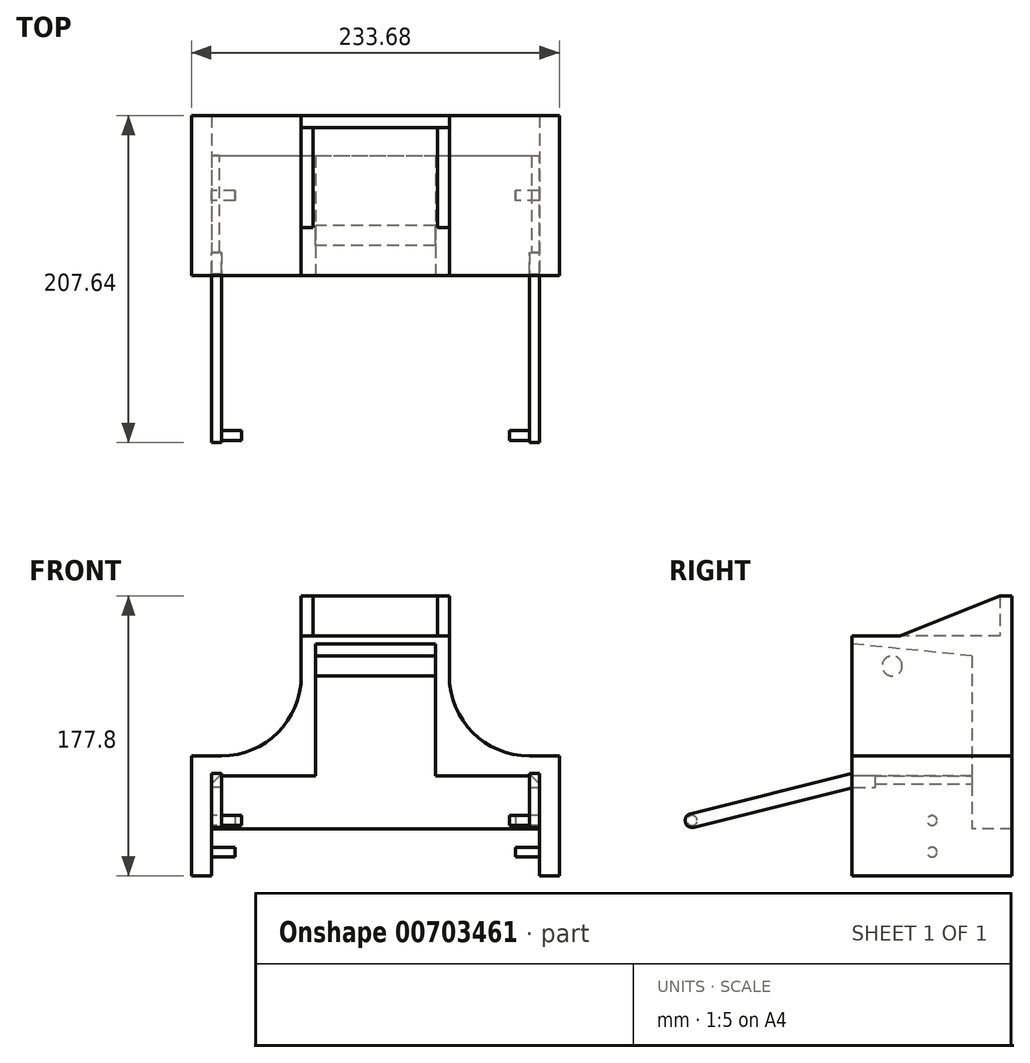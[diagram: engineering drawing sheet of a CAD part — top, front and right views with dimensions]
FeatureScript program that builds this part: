
annotation { "Feature Type Name" : "Feature", "Feature Type Description" : "" }
export const myFeature = defineFeature(function(context is Context, id is Id, definition is map)
    precondition{}
    {
        {
            var Q0;
            Q0=qCreatedBy(makeId("Front.planeOp"),FACE);
            var sketch = newSketch(context, id + "F0", { "sketchPlane" : qUnion([Q0])});
            skLineSegment(sketch, "E0.bottom", {"start": v(116.84, 76.2) * mm, "end": v(-116.84, 76.2) * mm});
            skLineSegment(sketch, "E0.top", {"start": v(116.84, -76.2) * mm, "end": v(-116.84, -76.2) * mm});
            skLineSegment(sketch, "E0.left", {"start": v(116.84, 76.2) * mm, "end": v(116.84, -76.2) * mm});
            skLineSegment(sketch, "E0.right", {"start": v(-116.84, 76.2) * mm, "end": v(-116.84, -76.2) * mm});
            skPoint(sketch, "E0.middle", {"position": v(0, 0) * mm});
            skLineSegment(sketch, "E1", {"start": v(-116.84, 0) * mm, "end": v(0, 0) * mm});
            skLineSegment(sketch, "E2", {"start": v(116.84, 0) * mm, "end": v(0, 0) * mm});
            skLineSegment(sketch, "E3", {"start": v(0, 76.2) * mm, "end": v(0, 0) * mm});
            skLineSegment(sketch, "E4", {"start": v(0, 0) * mm, "end": v(0, -76.2) * mm});
            skSolve(sketch);
        }
        {
            var Q0;
            Q0 = qSketchRegion(id + "F0", true);
            extrude(context, id + "F1", {"entities" : qUnion([Q0]), "oppositeDirection" : true, "depth" : 101.6 * mm, "offsetDistance" : 25.4 * mm});
        }
        {
            var Q0;
            Q0=makeQuery(id+"F1.opExtrude","CAP_FACE",FACE,{"disambiguationData":[OSD([sQuery(id+"F0.wireOp",EDGE,"E0.bottom"),sQuery(id+"F0.wireOp",EDGE,"E0.top"),sQuery(id+"F0.wireOp",EDGE,"E0.left"),sQuery(id+"F0.wireOp",EDGE,"E0.right")])],"isStart":true});
            var sketch = newSketch(context, id + "F2", { "sketchPlane" : qUnion([Q0])});
            skLineSegment(sketch, "E5.top", {"start": v(116.84, -76.2) * mm, "end": v(104.14, -76.2) * mm});
            skPoint(sketch, "E5.middle", {"position": v(0, 0) * mm});
            skLineSegment(sketch, "E6.0", {"start": v(-104.14, -12.7) * mm, "end": v(-104.14, -69.85) * mm});
            skLineSegment(sketch, "E6.2", {"start": v(104.14, -12.7) * mm, "end": v(104.14, -69.85) * mm});
            skLineSegment(sketch, "E7", {"start": v(-104.14, -12.7) * mm, "end": v(-38.1, -12.7) * mm});
            skLineSegment(sketch, "E8", {"start": v(-104.14, -69.85) * mm, "end": v(-104.14, -76.2) * mm});
            skLineSegment(sketch, "E9", {"start": v(104.14, -69.85) * mm, "end": v(104.14, -76.2) * mm});
            skLineSegment(sketch, "E10.trimOffspring", {"start": v(-104.14, -76.2) * mm, "end": v(-116.84, -76.2) * mm});
            skLineSegment(sketch, "E11.bottom", {"start": v(-38.1, 63.5) * mm, "end": v(38.1, 63.5) * mm});
            skLineSegment(sketch, "E11.left", {"start": v(-38.1, 63.5) * mm, "end": v(-38.1, -12.7) * mm});
            skLineSegment(sketch, "E11.right", {"start": v(38.1, 63.5) * mm, "end": v(38.1, -12.7) * mm});
            skPoint(sketch, "E11.top.start.orphan", {"position": v(-38.1, -63.5) * mm});
            skPoint(sketch, "E12.orphan", {"position": v(38.1, -63.5) * mm});
            skLineSegment(sketch, "E13.trimOffspring", {"start": v(38.1, -12.7) * mm, "end": v(104.14, -12.7) * mm});
            skLineSegment(sketch, "E14", {"start": v(-104.14, -76.2) * mm, "end": v(104.14, -76.2) * mm});
            skPoint(sketch, "E5.bottom.end.orphan", {"position": v(-116.84, 76.2) * mm});
            skPoint(sketch, "E5.bottom.start.orphan", {"position": v(116.84, 76.2) * mm});
            skSolve(sketch);
        }
        {
            var Q0;
            Q0 = qSketchRegion(id + "F2", true);
            extrude(context, id + "F3", {"entities" : qUnion([Q0]), "operationType" : NewBodyOperationType.REMOVE, "oppositeDirection" : true, "depth" : 76.2 * mm, "offsetDistance" : 25.4 * mm});
        }
        {
            var Q0;
            Q0=qCreatedBy(makeId("Right.planeOp"),FACE);
            var sketch = newSketch(context, id + "F4", { "sketchPlane" : qUnion([Q0])});
            skLineSegment(sketch, "E15", {"start": v(0, 63.5) * mm, "end": v(76.2, 63.5) * mm});
            skLineSegment(sketch, "E16", {"start": v(0, 63.5) * mm, "end": v(0, 71.12) * mm});
            skLineSegment(sketch, "E17", {"start": v(76.2, 63.5) * mm, "end": v(0, 71.12) * mm});
            skSolve(sketch);
        }
        {
            var Q0;
            Q0 = qSketchRegion(id + "F4", true);
            extrude(context, id + "F5", {"entities" : qUnion([Q0]), "operationType" : NewBodyOperationType.REMOVE, "oppositeDirection" : true, "depth" : 38.1 * mm, "offsetDistance" : 25.4 * mm, "hasSecondDirection" : true, "secondDirectionOppositeDirection" : false, "secondDirectionDepth" : 38.1 * mm});
        }
        {
            var Q0;
            Q0=qCreatedBy(makeId("Right.planeOp"),FACE);
            var sketch = newSketch(context, id + "F6", { "sketchPlane" : qUnion([Q0])});
            skCircle(sketch, "E18", {"center": v(25.4, 57.15) * mm, "radius": 6.35 * mm});
            skPoint(sketch, "E19.end.orphan", {"position": v(-5.3, 18.87) * mm});
            skPoint(sketch, "E19.start.orphan", {"position": v(0, 1.18) * mm});
            skLineSegment(sketch, "E20", {"start": v(25.4, 57.15) * mm, "end": v(25.4, 50.8) * mm});
            skCircle(sketch, "E21", {"center": v(50.8, -41.02) * mm, "radius": 3.11 * mm});
            skCircle(sketch, "E22", {"center": v(50.8, -61.09) * mm, "radius": 3.11 * mm});
            skSolve(sketch);
        }
        {
            var Q0;
            Q0 = qSketchRegion(id + "F6", true);
            extrude(context, id + "F7", {"entities" : qUnion([Q0]), "operationType" : NewBodyOperationType.ADD, "depth" : 114.3 * mm, "offsetDistance" : 25.4 * mm, "hasSecondDirection" : true, "secondDirectionOppositeDirection" : true, "secondDirectionDepth" : 114.3 * mm});
        }
        {
            var Q0;
            Q0=makeQuery(id+"F1.opExtrude","CAP_FACE",FACE,{"disambiguationData":[OSD([sQuery(id+"F0.wireOp",EDGE,"E0.bottom"),sQuery(id+"F0.wireOp",EDGE,"E0.top"),sQuery(id+"F0.wireOp",EDGE,"E0.left"),sQuery(id+"F0.wireOp",EDGE,"E0.right")])],"isStart":true});
            var sketch = newSketch(context, id + "F8", { "sketchPlane" : qUnion([Q0])});
            skLineSegment(sketch, "E23", {"start": v(-116.84, 76.2) * mm, "end": v(-46.99, 76.2) * mm});
            skLineSegment(sketch, "E24", {"start": v(116.84, 76.2) * mm, "end": v(116.84, 0) * mm});
            skLineSegment(sketch, "E25", {"start": v(-116.84, 76.2) * mm, "end": v(-116.84, 0) * mm});
            skLineSegment(sketch, "E26", {"start": v(-116.84, 0) * mm, "end": v(-97.79, 0) * mm});
            skLineSegment(sketch, "E27", {"start": v(-46.99, 50.8) * mm, "end": v(-46.99, 76.2) * mm});
            skLineSegment(sketch, "E28", {"start": v(116.84, 0) * mm, "end": v(97.79, 0) * mm});
            skLineSegment(sketch, "E29", {"start": v(46.99, 50.8) * mm, "end": v(46.99, 76.2) * mm});
            skPoint(sketch, "E30.visualSharp", {"position": v(-46.99, 0) * mm});
            skArc(sketch, "E30.filletArc", {"start": v(-97.79, 0) * mm, "mid": v(-61.87, 14.88) * mm, "end": v(-46.99, 50.8) * mm});
            skPoint(sketch, "E31.visualSharp", {"position": v(46.99, 0) * mm});
            skArc(sketch, "E31.filletArc", {"start": v(46.99, 50.8) * mm, "mid": v(61.87, 14.88) * mm, "end": v(97.79, 0) * mm});
            skLineSegment(sketch, "E32.trimOffspring", {"start": v(47, 76.2) * mm, "end": v(116.84, 76.2) * mm});
            skSolve(sketch);
        }
        {
            var Q0;
            Q0 = qSketchRegion(id + "F8", true);
            extrude(context, id + "F9", {"entities" : qUnion([Q0]), "operationType" : NewBodyOperationType.REMOVE, "endBound" : BoundingType.THROUGH_ALL, "oppositeDirection" : true, "depth" : 25.4 * mm, "offsetDistance" : 25.4 * mm});
        }
        {
            var Q0;
            Q0=makeQuery(id+"F3.boolean.opBoolean","COPY",FACE,{"derivedFrom":makeQuery(id+"F3.opExtrude","CAP_FACE",FACE,{"disambiguationData":[OSD([sQuery(id+"F2.wireOp",EDGE,"E6.0"),sQuery(id+"F2.wireOp",EDGE,"E6.2"),sQuery(id+"F2.wireOp",EDGE,"E7"),sQuery(id+"F2.wireOp",EDGE,"E8"),sQuery(id+"F2.wireOp",EDGE,"E9"),sQuery(id+"F2.wireOp",EDGE,"E11.bottom"),sQuery(id+"F2.wireOp",EDGE,"E11.left"),sQuery(id+"F2.wireOp",EDGE,"E11.right"),sQuery(id+"F2.wireOp",EDGE,"E13.trimOffspring"),sQuery(id+"F2.wireOp",EDGE,"E14")])],"isStart":false})});
            var sketch = newSketch(context, id + "F10", { "sketchPlane" : qUnion([Q0])});
            skLineSegment(sketch, "E33", {"start": v(104.14, -48.77) * mm, "end": v(104.14, -76.2) * mm});
            skLineSegment(sketch, "E34", {"start": v(104.14, -76.2) * mm, "end": v(-104.14, -76.2) * mm});
            skLineSegment(sketch, "E35", {"start": v(-104.14, -76.2) * mm, "end": v(-104.14, -48.77) * mm});
            skLineSegment(sketch, "E36.0", {"start": v(-104.14, -46.23) * mm, "end": v(104.14, -46.23) * mm});
            skLineSegment(sketch, "E37", {"start": v(-104.14, -48.77) * mm, "end": v(-104.14, -46.23) * mm});
            skLineSegment(sketch, "E38", {"start": v(104.14, -48.77) * mm, "end": v(104.14, -46.23) * mm});
            skSolve(sketch);
        }
        {
            var Q0;
            Q0 = qSketchRegion(id + "F10", true);
            extrude(context, id + "F11", {"entities" : qUnion([Q0]), "operationType" : NewBodyOperationType.REMOVE, "endBound" : BoundingType.THROUGH_ALL, "oppositeDirection" : true, "depth" : 25.4 * mm, "offsetDistance" : 25.4 * mm});
        }
        {
            var Q0;
            Q0=makeQuery(id+"F11.boolean.opBoolean","MERGE",EDGE,{"derivedFrom":[makeQuery(id+"F3.boolean.opBoolean","COPY",EDGE,{"derivedFrom":makeQuery(id+"F3.opExtrude","SWEPT_EDGE",EDGE,{"disambiguationData":[OSD([sQuery(id+"F2.wireOp",EDGE,"E6.0"),sQuery(id+"F2.wireOp",EDGE,"E7")])]})}),makeQuery(id+"F11.opExtrude","SWEPT_EDGE",EDGE,{"disambiguationData":[OSD([sQuery(id+"F10.wireOp",EDGE,"ZN3Ngnv2-gBWY-LndC-JIqI-UH5rID8Ztq4W"),sQuery(id+"F10.wireOp",EDGE,"E35")])]})]});
            var Q1;
            Q1=makeQuery(id+"F11.boolean.opBoolean","MERGE",EDGE,{"derivedFrom":[makeQuery(id+"F3.boolean.opBoolean","COPY",EDGE,{"derivedFrom":makeQuery(id+"F3.opExtrude","SWEPT_EDGE",EDGE,{"disambiguationData":[OSD([sQuery(id+"F2.wireOp",EDGE,"E6.2"),sQuery(id+"F2.wireOp",EDGE,"E13.trimOffspring")])]})}),makeQuery(id+"F11.opExtrude","SWEPT_EDGE",EDGE,{"disambiguationData":[OSD([sQuery(id+"F10.wireOp",EDGE,"ZN3Ngnv2-gBWY-LndC-JIqI-UH5rID8Ztq4W"),sQuery(id+"F10.wireOp",EDGE,"E33")])]})]});
            chamfer(context, id + "F12", {"entities" : qUnion([Q0, Q1]), "width" : 5.08 * mm, "tangentPropagation" : true});
        }
        {
            var Q0;
            Q0=qCreatedBy(makeId("Front.planeOp"),FACE);
            var sketch = newSketch(context, id + "F13", { "sketchPlane" : qUnion([Q0])});
            skLineSegment(sketch, "E39.bottom", {"start": v(-88.9, -24.7) * mm, "end": v(88.9, -24.7) * mm});
            skLineSegment(sketch, "E39.top", {"start": v(-88.9, -86.9) * mm, "end": v(88.9, -86.9) * mm});
            skLineSegment(sketch, "E39.left", {"start": v(-88.9, -24.7) * mm, "end": v(-88.9, -86.9) * mm});
            skLineSegment(sketch, "E39.right", {"start": v(88.9, -24.7) * mm, "end": v(88.9, -86.9) * mm});
            skPoint(sketch, "E39.middle", {"position": v(0, -55.8) * mm});
            skPoint(sketch, "E40.orphan", {"position": v(0, 1.98) * mm});
            skSolve(sketch);
        }
        {
            var Q0;
            Q0 = qSketchRegion(id + "F13", true);
            extrude(context, id + "F14", {"entities" : qUnion([Q0]), "operationType" : NewBodyOperationType.REMOVE, "oppositeDirection" : true, "depth" : 76.2 * mm, "offsetDistance" : 25.4 * mm});
        }
        {
            var Q0;
            Q0=makeQuery(id+"F1.opExtrude","SWEPT_FACE",FACE,{"disambiguationData":[OSD([sQuery(id+"F0.wireOp",EDGE,"E0.bottom")])]});
            var sketch = newSketch(context, id + "F15", { "sketchPlane" : qUnion([Q0])});
            skLineSegment(sketch, "E41", {"start": v(-47, 101.6) * mm, "end": v(46.99, 101.6) * mm});
            skLineSegment(sketch, "E42", {"start": v(46.99, 101.6) * mm, "end": v(46.99, 93.98) * mm});
            skLineSegment(sketch, "E43", {"start": v(46.99, 93.98) * mm, "end": v(-46.99, 93.98) * mm});
            skLineSegment(sketch, "E44", {"start": v(-46.99, 93.98) * mm, "end": v(-47, 101.6) * mm});
            skSolve(sketch);
        }
        {
            var Q0;
            Q0 = qSketchRegion(id + "F15", true);
            extrude(context, id + "F16", {"entities" : qUnion([Q0]), "operationType" : NewBodyOperationType.ADD, "depth" : 25.4 * mm, "offsetDistance" : 25.4 * mm});
        }
        {
            var Q0;
            Q0=makeQuery(id+"F16.boolean.opBoolean","MERGE",FACE,{"derivedFrom":[makeQuery(id+"F9.boolean.opBoolean","COPY",FACE,{"derivedFrom":makeQuery(id+"F9.opExtrude","SWEPT_FACE",FACE,{"disambiguationData":[OSD([sQuery(id+"F8.wireOp",EDGE,"E29")])]})}),makeQuery(id+"F16.opExtrude","SWEPT_FACE",FACE,{"disambiguationData":[OSD([sQuery(id+"F15.wireOp",EDGE,"E42")])]})]});
            var sketch = newSketch(context, id + "F17", { "sketchPlane" : qUnion([Q0])});
            skLineSegment(sketch, "E45", {"start": v(93.98, 101.6) * mm, "end": v(93.98, 76.2) * mm});
            skLineSegment(sketch, "E46", {"start": v(93.98, 76.2) * mm, "end": v(30.48, 76.2) * mm});
            skLineSegment(sketch, "E47", {"start": v(30.48, 76.2) * mm, "end": v(93.98, 101.6) * mm});
            skSolve(sketch);
        }
        {
            var Q0;
            Q0 = qSketchRegion(id + "F17", true);
            extrude(context, id + "F18", {"entities" : qUnion([Q0]), "operationType" : NewBodyOperationType.ADD, "oppositeDirection" : true, "depth" : 7.62 * mm, "offsetDistance" : 25.4 * mm});
        }
        {
            var Q0;
            Q0=makeQuery(id+"F16.boolean.opBoolean","MERGE",FACE,{"derivedFrom":[makeQuery(id+"F9.boolean.opBoolean","COPY",FACE,{"derivedFrom":makeQuery(id+"F9.opExtrude","SWEPT_FACE",FACE,{"disambiguationData":[OSD([sQuery(id+"F8.wireOp",EDGE,"E27")])]})}),makeQuery(id+"F16.opExtrude","SWEPT_FACE",FACE,{"disambiguationData":[OSD([sQuery(id+"F15.wireOp",EDGE,"E44")])]})]});
            var sketch = newSketch(context, id + "F19", { "sketchPlane" : qUnion([Q0])});
            skLineSegment(sketch, "E48", {"start": v(-93.98, 101.6) * mm, "end": v(-93.98, 76.2) * mm});
            skLineSegment(sketch, "E49", {"start": v(-93.98, 76.2) * mm, "end": v(-30.48, 76.2) * mm});
            skLineSegment(sketch, "E50", {"start": v(-93.98, 101.6) * mm, "end": v(-30.48, 76.2) * mm});
            skSolve(sketch);
        }
        {
            var Q0;
            Q0 = qSketchRegion(id + "F19", true);
            extrude(context, id + "F20", {"entities" : qUnion([Q0]), "operationType" : NewBodyOperationType.ADD, "oppositeDirection" : true, "depth" : 7.62 * mm, "offsetDistance" : 25.4 * mm});
        }
        {
            var Q0;
            Q0=makeQuery(id+"F11.boolean.opBoolean","MERGE",FACE,{"derivedFrom":[makeQuery(id+"F3.boolean.opBoolean","COPY",FACE,{"derivedFrom":makeQuery(id+"F3.opExtrude","SWEPT_FACE",FACE,{"disambiguationData":[OSD([sQuery(id+"F2.wireOp",EDGE,"E6.0"),sQuery(id+"F2.wireOp",EDGE,"E8")])]})}),makeQuery(id+"F11.opExtrude","SWEPT_FACE",FACE,{"disambiguationData":[OSD([sQuery(id+"F10.wireOp",EDGE,"E35")])]})]});
            var sketch = newSketch(context, id + "F21", { "sketchPlane" : qUnion([Q0])});
            skLineSegment(sketch, "E51", {"start": v(0, -41.02) * mm, "end": v(0, -15.62) * mm});
            skPoint(sketch, "E52.start.orphan", {"position": v(50.8, -41.02) * mm});
            skCircle(sketch, "E53", {"center": v(-101.6, -41.02) * mm, "radius": 3.18 * mm});
            skLineSegment(sketch, "E54.0", {"start": v(-1.08, -11.3) * mm, "end": v(6.03, -9.53) * mm});
            skLineSegment(sketch, "E54.1", {"start": v(-102.68, -36.7) * mm, "end": v(-1.08, -11.3) * mm});
            skArc(sketch, "E54.2", {"start": v(-102.68, -36.7) * mm, "mid": v(-105.91, -42.1) * mm, "end": v(-100.52, -45.33) * mm});
            skLineSegment(sketch, "E54.3", {"start": v(-100.52, -45.33) * mm, "end": v(1.08, -19.93) * mm});
            skPoint(sketch, "E55.start.orphan", {"position": v(27.71, -4.6) * mm});
            skPoint(sketch, "E56.end.orphan", {"position": v(4.8, -4.6) * mm});
            skLineSegment(sketch, "E57", {"start": v(1.08, -19.93) * mm, "end": v(14.64, -19.93) * mm});
            skLineSegment(sketch, "E58", {"start": v(14.64, -19.93) * mm, "end": v(14.64, -9.53) * mm});
            skLineSegment(sketch, "E59", {"start": v(14.64, -9.53) * mm, "end": v(6.03, -9.53) * mm});
            skSolve(sketch);
        }
        {
            var Q0;
            Q0 = qSketchRegion(id + "F21", true);
            var Q1;
            Q1=makeQuery(id+"F21.imprint","IMPRINT",FACE,{"disambiguationData":[TD([[makeQuery(id+"F21.imprint","IMPRINT",EDGE,{"derivedFrom":sQuery(id+"F21.wireOp",EDGE,"E53")}),1.0]])]});
            extrude(context, id + "F22", {"entities" : qUnion([Q0, Q1]), "operationType" : NewBodyOperationType.ADD, "depth" : 6.35 * mm, "offsetDistance" : 25.4 * mm});
        }
        {
            var Q0;
            Q0=makeQuery(id+"F21.imprint","IMPRINT",FACE,{"disambiguationData":[TD([[makeQuery(id+"F21.imprint","IMPRINT",EDGE,{"derivedFrom":sQuery(id+"F21.wireOp",EDGE,"E53")}),1.0]])]});
            extrude(context, id + "F23", {"entities" : qUnion([Q0]), "operationType" : NewBodyOperationType.ADD, "depth" : 19.05 * mm, "offsetDistance" : 25.4 * mm});
        }
        {
            var Q0;
            Q0=makeQuery(id+"F1.opExtrude","SWEPT_BODY",BODY,{"disambiguationData":[OSD([sQuery(id+"F0.wireOp",EDGE,"E0.bottom"),sQuery(id+"F0.wireOp",EDGE,"E0.top"),sQuery(id+"F0.wireOp",EDGE,"E0.left"),sQuery(id+"F0.wireOp",EDGE,"E0.right")])]});
            var Q1;
            Q1=qCreatedBy(makeId("Right.planeOp"),FACE);
            mirror(context, id + "F24", {"operationType" : NewBodyOperationType.ADD, "entities" : qUnion([Q0]), "mirrorPlane" : qUnion([Q1])});
        }
    });
